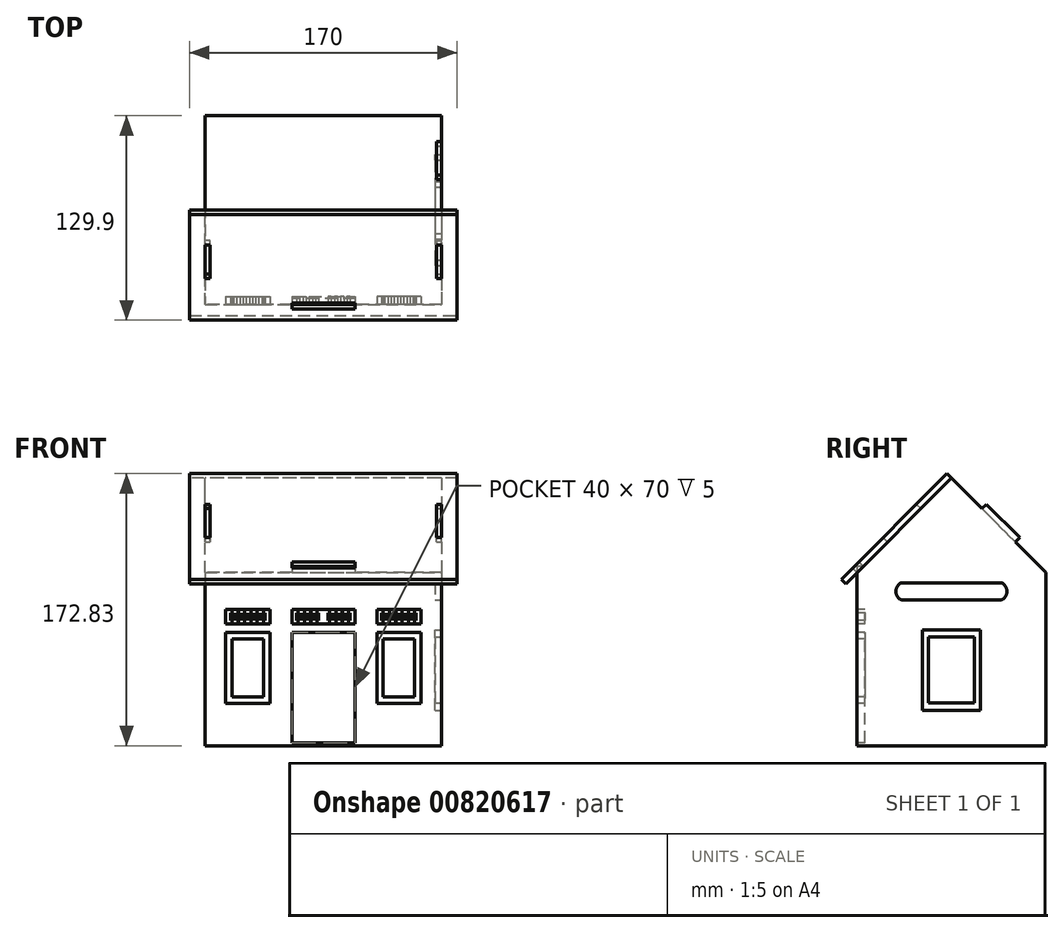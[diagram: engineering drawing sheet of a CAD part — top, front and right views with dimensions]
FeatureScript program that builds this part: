
annotation { "Feature Type Name" : "Feature", "Feature Type Description" : "" }
export const myFeature = defineFeature(function(context is Context, id is Id, definition is map)
    precondition{}
    {
        {
            var Q0;
            Q0=qCreatedBy(makeId("Top.planeOp"),FACE);
            var sketch = newSketch(context, id + "F0", { "sketchPlane" : qUnion([Q0])});
            skLineSegment(sketch, "E0.bottom", {"start": v(-75, 60) * mm, "end": v(75, 60) * mm});
            skLineSegment(sketch, "E0.top", {"start": v(-75, -60) * mm, "end": v(75, -60) * mm});
            skLineSegment(sketch, "E0.left", {"start": v(-75, 60) * mm, "end": v(-75, -60) * mm});
            skLineSegment(sketch, "E0.right", {"start": v(75, 60) * mm, "end": v(75, -60) * mm});
            skPoint(sketch, "E0.middle", {"position": v(0, 0) * mm});
            skSolve(sketch);
        }
        {
            var Q0;
            Q0=makeQuery(id+"F0.imprint","IMPRINT",FACE,{"disambiguationData":[TD([[makeQuery(id+"F0.imprint","IMPRINT",EDGE,{"derivedFrom":sQuery(id+"F0.wireOp",EDGE,"E0.bottom")}),-1.0]])]});
            extrude(context, id + "F1", {"entities" : qUnion([Q0]), "depth" : 170 * mm, "offsetDistance" : 25 * mm});
        }
        {
            var Q0;
            Q0=makeQuery(id+"F1.opExtrude","CAP_EDGE",EDGE,{"disambiguationData":[OSD([sQuery(id+"F0.wireOp",EDGE,"E0.top")])],"isStart":false});
            var Q1;
            Q1=makeQuery(id+"F1.opExtrude","CAP_EDGE",EDGE,{"disambiguationData":[OSD([sQuery(id+"F0.wireOp",EDGE,"E0.bottom")])],"isStart":false});
            chamfer(context, id + "F2", {"entities" : qUnion([Q0, Q1]), "width" : 60 * mm, "tangentPropagation" : true});
        }
        {
            var Q0;
            Q0=makeQuery(id+"F1.opExtrude","SWEPT_FACE",FACE,{"disambiguationData":[OSD([sQuery(id+"F0.wireOp",EDGE,"E0.top")])]});
            var sketch = newSketch(context, id + "F3", { "sketchPlane" : qUnion([Q0])});
            skLineSegment(sketch, "E1.bottom", {"start": v(20, 2) * mm, "end": v(-20, 2) * mm});
            skLineSegment(sketch, "E1.top", {"start": v(20, 72) * mm, "end": v(-20, 72) * mm});
            skLineSegment(sketch, "E1.left", {"start": v(20, 2) * mm, "end": v(20, 72) * mm});
            skLineSegment(sketch, "E1.right", {"start": v(-20, 2) * mm, "end": v(-20, 72) * mm});
            skPoint(sketch, "E1.middle", {"position": v(0, 37) * mm});
            skLineSegment(sketch, "E2.bottom", {"start": v(-62, 72) * mm, "end": v(-34, 72) * mm});
            skLineSegment(sketch, "E2.top", {"start": v(-62, 27) * mm, "end": v(-34, 27) * mm});
            skLineSegment(sketch, "E2.left", {"start": v(-62, 72) * mm, "end": v(-62, 27) * mm});
            skLineSegment(sketch, "E2.right", {"start": v(-34, 72) * mm, "end": v(-34, 27) * mm});
            skLineSegment(sketch, "E3.bottom", {"start": v(-62, 77.54) * mm, "end": v(-34, 77.54) * mm});
            skLineSegment(sketch, "E3.top", {"start": v(-62, 86.55) * mm, "end": v(-34, 86.55) * mm});
            skLineSegment(sketch, "E3.left", {"start": v(-62, 77.54) * mm, "end": v(-62, 86.55) * mm});
            skLineSegment(sketch, "E3.right", {"start": v(-34, 77.54) * mm, "end": v(-34, 86.55) * mm});
            skLineSegment(sketch, "E4.bottom", {"start": v(-20, 77.54) * mm, "end": v(20, 77.54) * mm});
            skLineSegment(sketch, "E4.top", {"start": v(-20, 86.55) * mm, "end": v(20, 86.55) * mm});
            skLineSegment(sketch, "E4.left", {"start": v(-20, 77.54) * mm, "end": v(-20, 86.55) * mm});
            skLineSegment(sketch, "E4.right", {"start": v(20, 77.54) * mm, "end": v(20, 86.55) * mm});
            skLineSegment(sketch, "E5.0", {"start": v(-58, 68) * mm, "end": v(-58, 31) * mm});
            skLineSegment(sketch, "E5.1", {"start": v(-58, 68) * mm, "end": v(-38, 68) * mm});
            skLineSegment(sketch, "E5.2", {"start": v(-38, 68) * mm, "end": v(-38, 31) * mm});
            skLineSegment(sketch, "E5.3", {"start": v(-58, 31) * mm, "end": v(-38, 31) * mm});
            skLineSegment(sketch, "E6.bottom", {"start": v(20, 114) * mm, "end": v(-20, 114) * mm});
            skLineSegment(sketch, "E6.top", {"start": v(20, 106) * mm, "end": v(-20, 106) * mm});
            skLineSegment(sketch, "E6.left", {"start": v(20, 114) * mm, "end": v(20, 106) * mm});
            skLineSegment(sketch, "E6.right", {"start": v(-20, 114) * mm, "end": v(-20, 106) * mm});
            skPoint(sketch, "E6.middle", {"position": v(0, 110) * mm});
            skLineSegment(sketch, "E7.bottom", {"start": v(-59, 84.55) * mm, "end": v(-57, 84.55) * mm});
            skLineSegment(sketch, "E7.top", {"start": v(-59, 79.54) * mm, "end": v(-57, 79.54) * mm});
            skLineSegment(sketch, "E7.left", {"start": v(-59, 84.55) * mm, "end": v(-59, 79.54) * mm});
            skLineSegment(sketch, "E7.right", {"start": v(-57, 84.55) * mm, "end": v(-57, 79.54) * mm});
            skLineSegment(sketch, "E8.1.0.0", {"start": v(-55, 84.55) * mm, "end": v(-53, 84.55) * mm});
            skLineSegment(sketch, "E8.1.0.1", {"start": v(-53, 84.55) * mm, "end": v(-53, 79.54) * mm});
            skLineSegment(sketch, "E8.1.0.2", {"start": v(-55, 79.54) * mm, "end": v(-53, 79.54) * mm});
            skLineSegment(sketch, "E8.1.0.3", {"start": v(-55, 84.55) * mm, "end": v(-55, 79.54) * mm});
            skLineSegment(sketch, "E8.2.0.0", {"start": v(-51, 84.55) * mm, "end": v(-49, 84.55) * mm});
            skLineSegment(sketch, "E8.2.0.1", {"start": v(-49, 84.55) * mm, "end": v(-49, 79.54) * mm});
            skLineSegment(sketch, "E8.2.0.2", {"start": v(-51, 79.54) * mm, "end": v(-49, 79.54) * mm});
            skLineSegment(sketch, "E8.2.0.3", {"start": v(-51, 84.55) * mm, "end": v(-51, 79.54) * mm});
            skLineSegment(sketch, "E8.3.0.0", {"start": v(-47, 84.55) * mm, "end": v(-45, 84.55) * mm});
            skLineSegment(sketch, "E8.3.0.1", {"start": v(-45, 84.55) * mm, "end": v(-45, 79.54) * mm});
            skLineSegment(sketch, "E8.3.0.2", {"start": v(-47, 79.54) * mm, "end": v(-45, 79.54) * mm});
            skLineSegment(sketch, "E8.3.0.3", {"start": v(-47, 84.55) * mm, "end": v(-47, 79.54) * mm});
            skLineSegment(sketch, "E8.4.0.0", {"start": v(-43, 84.55) * mm, "end": v(-41, 84.55) * mm});
            skLineSegment(sketch, "E8.4.0.1", {"start": v(-41, 84.55) * mm, "end": v(-41, 79.54) * mm});
            skLineSegment(sketch, "E8.4.0.2", {"start": v(-43, 79.54) * mm, "end": v(-41, 79.54) * mm});
            skLineSegment(sketch, "E8.4.0.3", {"start": v(-43, 84.55) * mm, "end": v(-43, 79.54) * mm});
            skLineSegment(sketch, "E8.5.0.0", {"start": v(-39, 84.55) * mm, "end": v(-37, 84.55) * mm});
            skLineSegment(sketch, "E8.5.0.1", {"start": v(-37, 84.55) * mm, "end": v(-37, 79.54) * mm});
            skLineSegment(sketch, "E8.5.0.2", {"start": v(-39, 79.54) * mm, "end": v(-37, 79.54) * mm});
            skLineSegment(sketch, "E8.5.0.3", {"start": v(-39, 84.55) * mm, "end": v(-39, 79.54) * mm});
            skLineSegment(sketch, "E8.direction1", {"start": v(-59, 84.55) * mm, "end": v(-55, 84.55) * mm, "construction": true});
            skLineSegment(sketch, "E9", {"start": v(0, 72) * mm, "end": v(0, 37) * mm, "construction": true});
            skLineSegment(sketch, "E10.bottom", {"start": v(-17, 79.54) * mm, "end": v(-15, 79.54) * mm});
            skLineSegment(sketch, "E10.top", {"start": v(-17, 84.55) * mm, "end": v(-15, 84.55) * mm});
            skLineSegment(sketch, "E10.left", {"start": v(-17, 79.54) * mm, "end": v(-17, 84.55) * mm});
            skLineSegment(sketch, "E10.right", {"start": v(-15, 79.54) * mm, "end": v(-15, 84.55) * mm});
            skLineSegment(sketch, "E11.1.0.0", {"start": v(-13, 84.55) * mm, "end": v(-11, 84.55) * mm});
            skLineSegment(sketch, "E11.1.0.1", {"start": v(-13, 79.54) * mm, "end": v(-13, 84.55) * mm});
            skLineSegment(sketch, "E11.1.0.2", {"start": v(-11, 79.54) * mm, "end": v(-11, 84.55) * mm});
            skLineSegment(sketch, "E11.1.0.3", {"start": v(-13, 79.54) * mm, "end": v(-11, 79.54) * mm});
            skLineSegment(sketch, "E11.2.0.0", {"start": v(-9, 84.55) * mm, "end": v(-7, 84.55) * mm});
            skLineSegment(sketch, "E11.2.0.1", {"start": v(-9, 79.54) * mm, "end": v(-9, 84.55) * mm});
            skLineSegment(sketch, "E11.2.0.2", {"start": v(-7, 79.54) * mm, "end": v(-7, 84.55) * mm});
            skLineSegment(sketch, "E11.2.0.3", {"start": v(-9, 79.54) * mm, "end": v(-7, 79.54) * mm});
            skLineSegment(sketch, "E11.3.0.0", {"start": v(-5, 84.55) * mm, "end": v(-3, 84.55) * mm});
            skLineSegment(sketch, "E11.3.0.1", {"start": v(-5, 79.54) * mm, "end": v(-5, 84.55) * mm});
            skLineSegment(sketch, "E11.3.0.2", {"start": v(-3, 79.54) * mm, "end": v(-3, 84.55) * mm});
            skLineSegment(sketch, "E11.3.0.3", {"start": v(-5, 79.54) * mm, "end": v(-3, 79.54) * mm});
            skLineSegment(sketch, "E11.direction1", {"start": v(-17, 84.55) * mm, "end": v(-13, 84.55) * mm, "construction": true});
            skLineSegment(sketch, "E12.MirrorCS", {"start": v(59, 84.55) * mm, "end": v(57, 84.55) * mm});
            skLineSegment(sketch, "E13.MirrorCS", {"start": v(51, 79.54) * mm, "end": v(49, 79.54) * mm});
            skLineSegment(sketch, "E14.MirrorCS", {"start": v(43, 79.54) * mm, "end": v(41, 79.54) * mm});
            skLineSegment(sketch, "E15.MirrorCS", {"start": v(57, 84.55) * mm, "end": v(57, 79.54) * mm});
            skLineSegment(sketch, "E16.MirrorCS", {"start": v(53, 84.55) * mm, "end": v(53, 79.54) * mm});
            skLineSegment(sketch, "E17.MirrorCS", {"start": v(51, 84.55) * mm, "end": v(49, 84.55) * mm});
            skLineSegment(sketch, "E18.MirrorCS", {"start": v(49, 84.55) * mm, "end": v(49, 79.54) * mm});
            skLineSegment(sketch, "E19.MirrorCS", {"start": v(51, 84.55) * mm, "end": v(51, 79.54) * mm});
            skLineSegment(sketch, "E20.MirrorCS", {"start": v(55, 79.54) * mm, "end": v(53, 79.54) * mm});
            skLineSegment(sketch, "E21.MirrorCS", {"start": v(55, 84.55) * mm, "end": v(55, 79.54) * mm});
            skLineSegment(sketch, "E22.MirrorCS", {"start": v(47, 79.54) * mm, "end": v(45, 79.54) * mm});
            skLineSegment(sketch, "E23.MirrorCS", {"start": v(55, 84.55) * mm, "end": v(53, 84.55) * mm});
            skLineSegment(sketch, "E24.MirrorCS", {"start": v(43, 84.55) * mm, "end": v(43, 79.54) * mm});
            skLineSegment(sketch, "E25.MirrorCS", {"start": v(43, 84.55) * mm, "end": v(41, 84.55) * mm});
            skLineSegment(sketch, "E26.MirrorCS", {"start": v(41, 84.55) * mm, "end": v(41, 79.54) * mm});
            skLineSegment(sketch, "E27.MirrorCS", {"start": v(47, 84.55) * mm, "end": v(45, 84.55) * mm});
            skLineSegment(sketch, "E28.MirrorCS", {"start": v(39, 79.54) * mm, "end": v(37, 79.54) * mm});
            skLineSegment(sketch, "E29.MirrorCS", {"start": v(45, 84.55) * mm, "end": v(45, 79.54) * mm});
            skLineSegment(sketch, "E30.MirrorCS", {"start": v(59, 84.55) * mm, "end": v(55, 84.55) * mm, "construction": true});
            skLineSegment(sketch, "E31.MirrorCS", {"start": v(47, 84.55) * mm, "end": v(47, 79.54) * mm});
            skLineSegment(sketch, "E32.MirrorCS", {"start": v(39, 84.55) * mm, "end": v(37, 84.55) * mm});
            skLineSegment(sketch, "E33.MirrorCS", {"start": v(39, 84.55) * mm, "end": v(39, 79.54) * mm});
            skLineSegment(sketch, "E34.MirrorCS", {"start": v(59, 79.54) * mm, "end": v(57, 79.54) * mm});
            skLineSegment(sketch, "E35.MirrorCS", {"start": v(37, 84.55) * mm, "end": v(37, 79.54) * mm});
            skLineSegment(sketch, "E36.MirrorCS", {"start": v(59, 84.55) * mm, "end": v(59, 79.54) * mm});
            skLineSegment(sketch, "E37.MirrorCS", {"start": v(62, 86.55) * mm, "end": v(34, 86.55) * mm});
            skLineSegment(sketch, "E38.MirrorCS", {"start": v(62, 77.54) * mm, "end": v(34, 77.54) * mm});
            skLineSegment(sketch, "E39.MirrorCS", {"start": v(34, 77.54) * mm, "end": v(34, 86.55) * mm});
            skLineSegment(sketch, "E40.MirrorCS", {"start": v(62, 77.54) * mm, "end": v(62, 86.55) * mm});
            skLineSegment(sketch, "E41.MirrorCS", {"start": v(17, 84.55) * mm, "end": v(15, 84.55) * mm});
            skLineSegment(sketch, "E42.MirrorCS", {"start": v(9, 79.54) * mm, "end": v(7, 79.54) * mm});
            skLineSegment(sketch, "E43.MirrorCS", {"start": v(17, 84.55) * mm, "end": v(13, 84.55) * mm, "construction": true});
            skLineSegment(sketch, "E44.MirrorCS", {"start": v(13, 84.55) * mm, "end": v(11, 84.55) * mm});
            skLineSegment(sketch, "E45.MirrorCS", {"start": v(17, 79.54) * mm, "end": v(17, 84.55) * mm});
            skLineSegment(sketch, "E46.MirrorCS", {"start": v(5, 79.54) * mm, "end": v(5, 84.55) * mm});
            skLineSegment(sketch, "E47.MirrorCS", {"start": v(7, 79.54) * mm, "end": v(7, 84.55) * mm});
            skLineSegment(sketch, "E48.MirrorCS", {"start": v(11, 79.54) * mm, "end": v(11, 84.55) * mm});
            skLineSegment(sketch, "E49.MirrorCS", {"start": v(9, 79.54) * mm, "end": v(9, 84.55) * mm});
            skLineSegment(sketch, "E50.MirrorCS", {"start": v(3, 79.54) * mm, "end": v(3, 84.55) * mm});
            skLineSegment(sketch, "E51.MirrorCS", {"start": v(9, 84.55) * mm, "end": v(7, 84.55) * mm});
            skLineSegment(sketch, "E52.MirrorCS", {"start": v(13, 79.54) * mm, "end": v(13, 84.55) * mm});
            skLineSegment(sketch, "E53.MirrorCS", {"start": v(5, 79.54) * mm, "end": v(3, 79.54) * mm});
            skLineSegment(sketch, "E54.MirrorCS", {"start": v(15, 79.54) * mm, "end": v(15, 84.55) * mm});
            skLineSegment(sketch, "E55.MirrorCS", {"start": v(5, 84.55) * mm, "end": v(3, 84.55) * mm});
            skLineSegment(sketch, "E56.MirrorCS", {"start": v(13, 79.54) * mm, "end": v(11, 79.54) * mm});
            skLineSegment(sketch, "E57.MirrorCS", {"start": v(17, 79.54) * mm, "end": v(15, 79.54) * mm});
            skLineSegment(sketch, "E58.MirrorCS", {"start": v(62, 72) * mm, "end": v(34, 72) * mm});
            skLineSegment(sketch, "E59.MirrorCS", {"start": v(34, 72) * mm, "end": v(34, 27) * mm});
            skLineSegment(sketch, "E60.MirrorCS", {"start": v(58, 31) * mm, "end": v(38, 31) * mm});
            skLineSegment(sketch, "E61.MirrorCS", {"start": v(62, 72) * mm, "end": v(62, 27) * mm});
            skLineSegment(sketch, "E62.MirrorCS", {"start": v(62, 27) * mm, "end": v(34, 27) * mm});
            skLineSegment(sketch, "E63.MirrorCS", {"start": v(38, 68) * mm, "end": v(38, 31) * mm});
            skLineSegment(sketch, "E64.MirrorCS", {"start": v(58, 68) * mm, "end": v(38, 68) * mm});
            skLineSegment(sketch, "E65.MirrorCS", {"start": v(58, 68) * mm, "end": v(58, 31) * mm});
            skSolve(sketch);
        }
        {
            var Q0;
            Q0=makeQuery(id+"F3.imprint","IMPRINT",FACE,{"disambiguationData":[TD([[makeQuery(id+"F3.imprint","IMPRINT",EDGE,{"derivedFrom":sQuery(id+"F3.wireOp",EDGE,"E3.bottom")}),1.0]])]});
            var Q1;
            Q1=makeQuery(id+"F3.imprint","IMPRINT",FACE,{"disambiguationData":[TD([[makeQuery(id+"F3.imprint","IMPRINT",EDGE,{"derivedFrom":sQuery(id+"F3.wireOp",EDGE,"E2.bottom")}),-1.0]])]});
            var Q2;
            Q2=makeQuery(id+"F3.imprint","IMPRINT",FACE,{"disambiguationData":[TD([[makeQuery(id+"F3.imprint","IMPRINT",EDGE,{"derivedFrom":sQuery(id+"F3.wireOp",EDGE,"E1.bottom")}),-1.0]])]});
            var Q3;
            Q3=makeQuery(id+"F3.imprint","IMPRINT",FACE,{"disambiguationData":[TD([[makeQuery(id+"F3.imprint","IMPRINT",EDGE,{"derivedFrom":sQuery(id+"F3.wireOp",EDGE,"E4.bottom")}),1.0]])]});
            var Q4;
            Q4=makeQuery(id+"F3.imprint","IMPRINT",FACE,{"disambiguationData":[TD([[makeQuery(id+"F3.imprint","IMPRINT",EDGE,{"derivedFrom":sQuery(id+"F3.wireOp",EDGE,"ji37NXTx-lIk6-Y559-omp6-w41L25hVZg7v.bottom")}),1.0]])]});
            var Q5;
            Q5=makeQuery(id+"F3.imprint","IMPRINT",FACE,{"disambiguationData":[TD([[makeQuery(id+"F3.imprint","IMPRINT",EDGE,{"derivedFrom":sQuery(id+"F3.wireOp",EDGE,"1dyTqxES-r5Co-RlE2-DoiD-IUAGq1z08tmz.bottom")}),-1.0]])]});
            var Q6;
            Q6=makeQuery(id+"F3.imprint","IMPRINT",FACE,{"disambiguationData":[TD([[makeQuery(id+"F3.imprint","IMPRINT",EDGE,{"derivedFrom":sQuery(id+"F3.wireOp",EDGE,"E12.MirrorCS")}),-1.0]])]});
            var Q7;
            Q7=makeQuery(id+"F3.imprint","IMPRINT",FACE,{"disambiguationData":[TD([[makeQuery(id+"F3.imprint","IMPRINT",EDGE,{"derivedFrom":sQuery(id+"F3.wireOp",EDGE,"E58.MirrorCS")}),1.0]])]});
            extrude(context, id + "F4", {"entities" : qUnion([Q0, Q1, Q2, Q3, Q4, Q5, Q6, Q7]), "operationType" : NewBodyOperationType.REMOVE, "oppositeDirection" : true, "depth" : 5 * mm, "offsetDistance" : 25 * mm});
        }
        {
            var Q0;
            {var subQ0=sQuery(id+"F3.wireOp",EDGE,"E6.bottom");Q0=makeQuery(id+"F3.imprint","IMPRINT",FACE,{"disambiguationData":[TD([[makeQuery(id+"F3.imprint","IMPRINT",EDGE,{"derivedFrom":subQ0}),1.0]])]});}
            extrude(context, id + "F5", {"entities" : qUnion([Q0]), "operationType" : NewBodyOperationType.ADD, "oppositeDirection" : true, "depth" : 4 * mm, "offsetDistance" : 25 * mm});
        }
        {
            var Q0;
            Q0=makeQuery(id+"F1.opExtrude","SWEPT_FACE",FACE,{"disambiguationData":[OSD([sQuery(id+"F0.wireOp",EDGE,"E0.right")])]});
            var sketch = newSketch(context, id + "F6", { "sketchPlane" : qUnion([Q0])});
            skLineSegment(sketch, "E66", {"start": v(-40.6, 129.4) * mm, "end": v(-43.44, 132.22) * mm});
            skLineSegment(sketch, "E67", {"start": v(-43.44, 132.22) * mm, "end": v(-22.22, 153.44) * mm});
            skLineSegment(sketch, "E68", {"start": v(-22.22, 153.44) * mm, "end": v(-19.4, 150.6) * mm});
            skLineSegment(sketch, "E69", {"start": v(-32.83, 142.83) * mm, "end": v(-30, 140) * mm, "construction": true});
            skLineSegment(sketch, "E70.bottom", {"start": v(18.33, 22.57) * mm, "end": v(-18.33, 22.57) * mm});
            skLineSegment(sketch, "E70.top", {"start": v(18.33, 73.63) * mm, "end": v(-18.33, 73.63) * mm});
            skLineSegment(sketch, "E70.left", {"start": v(18.33, 22.57) * mm, "end": v(18.33, 73.63) * mm});
            skLineSegment(sketch, "E70.right", {"start": v(-18.33, 22.57) * mm, "end": v(-18.33, 73.63) * mm});
            skPoint(sketch, "E70.middle", {"position": v(0, 48.1) * mm});
            skLineSegment(sketch, "E71.bottom", {"start": v(14.74, 69.05) * mm, "end": v(-14.74, 69.05) * mm});
            skLineSegment(sketch, "E71.top", {"start": v(14.74, 27.15) * mm, "end": v(-14.74, 27.15) * mm});
            skLineSegment(sketch, "E71.left", {"start": v(14.74, 69.05) * mm, "end": v(14.74, 27.15) * mm});
            skLineSegment(sketch, "E71.right", {"start": v(-14.74, 69.05) * mm, "end": v(-14.74, 27.15) * mm});
            skLineSegment(sketch, "E72", {"start": v(0, 170) * mm, "end": v(0, 73.63) * mm, "construction": true});
            skLineSegment(sketch, "E73.MirrorCS", {"start": v(43.44, 132.22) * mm, "end": v(22.22, 153.44) * mm});
            skLineSegment(sketch, "E74.MirrorCS", {"start": v(40.6, 129.4) * mm, "end": v(43.44, 132.22) * mm});
            skLineSegment(sketch, "E75.MirrorCS", {"start": v(22.22, 153.44) * mm, "end": v(19.4, 150.6) * mm});
            skLineSegment(sketch, "E76.bottom", {"start": v(31.79, 103.52) * mm, "end": v(-31.79, 103.52) * mm});
            skLineSegment(sketch, "E76.top", {"start": v(31.79, 92.61) * mm, "end": v(-31.79, 92.61) * mm});
            skLineSegment(sketch, "E76.left", {"start": v(31.79, 103.52) * mm, "end": v(31.79, 92.61) * mm});
            skLineSegment(sketch, "E76.right", {"start": v(-31.79, 103.52) * mm, "end": v(-31.79, 92.61) * mm});
            skPoint(sketch, "E76.middle", {"position": v(0, 98.07) * mm});
            skArc(sketch, "E77", {"start": v(-31.79, 103.52) * mm, "mid": v(-35.3, 98.07) * mm, "end": v(-31.79, 92.61) * mm});
            skArc(sketch, "E78.MirrorCS", {"start": v(31.79, 103.52) * mm, "mid": v(35.3, 98.07) * mm, "end": v(31.79, 92.61) * mm});
            skSolve(sketch);
        }
        {
            var Q0;
            Q0=makeQuery(id+"F6.imprint","IMPRINT",FACE,{"disambiguationData":[TD([[makeQuery(id+"F6.imprint","IMPRINT",EDGE,{"derivedFrom":sQuery(id+"F6.wireOp",EDGE,"E70.bottom")}),-1.0]])]});
            var Q1;
            Q1=makeQuery(id+"F6.imprint","IMPRINT",FACE,{"disambiguationData":[TD([[makeQuery(id+"F6.imprint","IMPRINT",EDGE,{"derivedFrom":sQuery(id+"F6.wireOp",EDGE,"E76.bottom")}),1.0]])]});
            var Q2;
            Q2=makeQuery(id+"F6.imprint","IMPRINT",FACE,{"disambiguationData":[TD([[makeQuery(id+"F6.imprint","IMPRINT",EDGE,{"derivedFrom":sQuery(id+"F6.wireOp",EDGE,"E76.right")}),-1.0]])]});
            var Q3;
            Q3=makeQuery(id+"F6.imprint","IMPRINT",FACE,{"disambiguationData":[TD([[makeQuery(id+"F6.imprint","IMPRINT",EDGE,{"derivedFrom":sQuery(id+"F6.wireOp",EDGE,"E76.left")}),1.0]])]});
            extrude(context, id + "F7", {"entities" : qUnion([Q0, Q1, Q2, Q3]), "operationType" : NewBodyOperationType.REMOVE, "oppositeDirection" : true, "depth" : 4 * mm, "offsetDistance" : 25 * mm});
        }
        {
            var Q0;
            {var subQ0=sQuery(id+"F6.wireOp",EDGE,"E66");Q0=makeQuery(id+"F6.imprint","IMPRINT",FACE,{"disambiguationData":[TD([[makeQuery(id+"F6.imprint","IMPRINT",EDGE,{"derivedFrom":subQ0}),-1.0]])]});}
            var Q1;
            Q1=makeQuery(id+"F6.imprint","IMPRINT",FACE,{"disambiguationData":[TD([[makeQuery(id+"F6.imprint","IMPRINT",EDGE,{"derivedFrom":sQuery(id+"F6.wireOp",EDGE,"E73.MirrorCS")}),1.0]])]});
            extrude(context, id + "F8", {"entities" : qUnion([Q0, Q1]), "operationType" : NewBodyOperationType.ADD, "oppositeDirection" : true, "depth" : 3 * mm, "offsetDistance" : 25 * mm});
        }
        {
            var Q0;
            Q0=makeQuery(id+"F2.opChamfer","BLEND_FACE",FACE,{"disambiguationData":[OSD([sQuery(id+"F0.wireOp",EDGE,"E0.top")])]});
            var sketch = newSketch(context, id + "F9", { "sketchPlane" : qUnion([Q0])});
            skLineSegment(sketch, "E79.0.0", {"start": v(75, 62.78) * mm, "end": v(72, 62.78) * mm});
            skLineSegment(sketch, "E79.0.1", {"start": v(72, 62.78) * mm, "end": v(72, 92.78) * mm});
            skLineSegment(sketch, "E79.0.2", {"start": v(72, 92.78) * mm, "end": v(75, 92.78) * mm});
            skLineSegment(sketch, "E79.0.3", {"start": v(75, 92.78) * mm, "end": v(75, 120.2) * mm});
            skLineSegment(sketch, "E79.0.4", {"start": v(75, 120.2) * mm, "end": v(-75, 120.2) * mm});
            skLineSegment(sketch, "E79.0.5", {"start": v(-75, 120.2) * mm, "end": v(-75, 35.36) * mm});
            skLineSegment(sketch, "E79.0.6", {"start": v(-75, 35.36) * mm, "end": v(-20, 35.36) * mm});
            skLineSegment(sketch, "E79.0.7", {"start": v(-20, 35.36) * mm, "end": v(-20, 41.01) * mm});
            skLineSegment(sketch, "E79.0.8", {"start": v(-20, 41.01) * mm, "end": v(20, 41.01) * mm});
            skLineSegment(sketch, "E79.0.9", {"start": v(20, 41.01) * mm, "end": v(20, 35.36) * mm});
            skLineSegment(sketch, "E79.0.10", {"start": v(20, 35.36) * mm, "end": v(75, 35.36) * mm});
            skLineSegment(sketch, "E79.0.11", {"start": v(75, 35.36) * mm, "end": v(75, 62.78) * mm});
            skLineSegment(sketch, "E80", {"start": v(-20, 35.36) * mm, "end": v(20, 35.36) * mm});
            skLineSegment(sketch, "E81", {"start": v(75, 62.78) * mm, "end": v(75, 92.78) * mm});
            skLineSegment(sketch, "E82", {"start": v(0, 120.2) * mm, "end": v(0, 35.36) * mm, "construction": true});
            skLineSegment(sketch, "E83.MirrorCS", {"start": v(-72, 62.78) * mm, "end": v(-72, 92.78) * mm});
            skLineSegment(sketch, "E84.MirrorCS", {"start": v(-72, 92.78) * mm, "end": v(-75, 92.78) * mm});
            skLineSegment(sketch, "E85.MirrorCS", {"start": v(-75, 62.78) * mm, "end": v(-72, 62.78) * mm});
            skLineSegment(sketch, "E86", {"start": v(75, 120.2) * mm, "end": v(85, 120.2) * mm});
            skLineSegment(sketch, "E87", {"start": v(85, 120.2) * mm, "end": v(85, 25.36) * mm});
            skLineSegment(sketch, "E88", {"start": v(85, 25.36) * mm, "end": v(0, 25.36) * mm});
            skLineSegment(sketch, "E89.MirrorCS", {"start": v(-75, 120.2) * mm, "end": v(-85, 120.2) * mm});
            skLineSegment(sketch, "E90.MirrorCS", {"start": v(-85, 120.2) * mm, "end": v(-85, 25.36) * mm});
            skLineSegment(sketch, "E91.MirrorCS", {"start": v(-85, 25.36) * mm, "end": v(0, 25.36) * mm});
            skSolve(sketch);
        }
        {
            var Q0;
            Q0=makeQuery(id+"F9.imprint","IMPRINT",FACE,{"disambiguationData":[TD([[makeQuery(id+"F9.imprint","IMPRINT",EDGE,{"derivedFrom":sQuery(id+"F9.wireOp",EDGE,"E79.0.0")}),-1.0]])]});
            var Q1;
            Q1=makeQuery(id+"F9.imprint","IMPRINT",FACE,{"disambiguationData":[TD([[makeQuery(id+"F9.imprint","IMPRINT",EDGE,{"derivedFrom":sQuery(id+"F9.wireOp",EDGE,"E79.0.3")}),1.0]])]});
            extrude(context, id + "F10", {"entities" : qUnion([Q0, Q1]), "depth" : 4 * mm, "offsetDistance" : 25 * mm});
        }
    });
